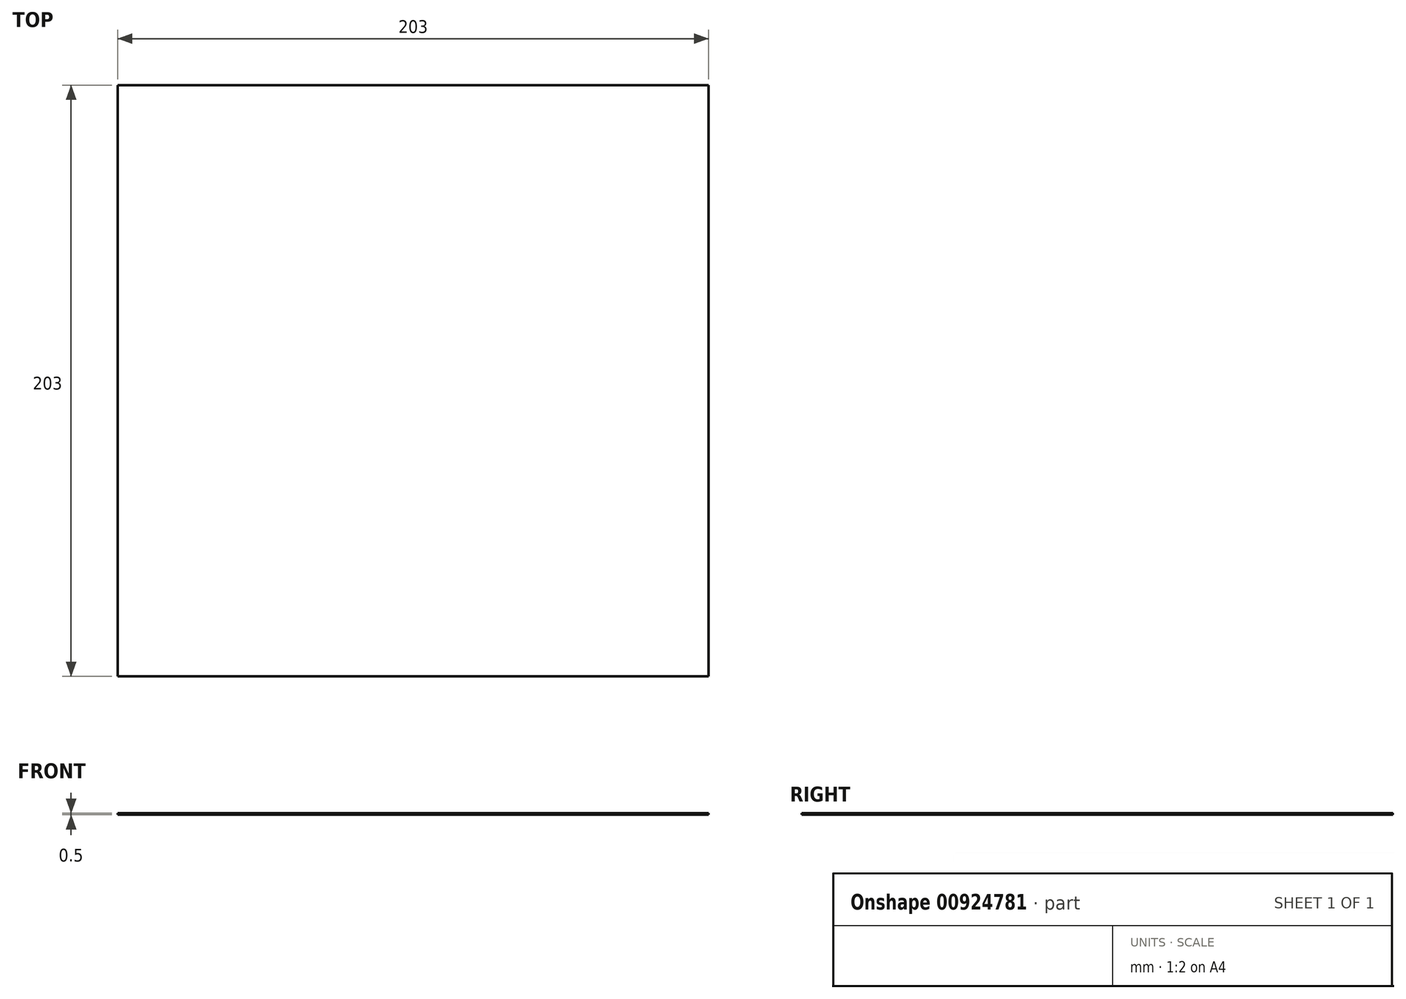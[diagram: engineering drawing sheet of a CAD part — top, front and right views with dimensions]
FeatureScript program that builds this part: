
annotation { "Feature Type Name" : "Feature", "Feature Type Description" : "" }
export const myFeature = defineFeature(function(context is Context, id is Id, definition is map)
    precondition{}
    {
        {
            var Q0;
            Q0=qCreatedBy(makeId("Top.planeOp"),FACE);
            var sketch = newSketch(context, id + "F0", { "sketchPlane" : qUnion([Q0])});
            skLineSegment(sketch, "E0.bottom", {"start": v(-103.23, -87.38) * mm, "end": v(99.77, -87.38) * mm});
            skLineSegment(sketch, "E0.top", {"start": v(-103.23, 115.62) * mm, "end": v(99.77, 115.62) * mm});
            skLineSegment(sketch, "E0.left", {"start": v(-103.23, -87.38) * mm, "end": v(-103.23, 115.62) * mm});
            skLineSegment(sketch, "E0.right", {"start": v(99.77, -87.38) * mm, "end": v(99.77, 115.62) * mm});
            skSolve(sketch);
        }
        {
            var Q0;
            Q0 = qSketchRegion(id + "F0", true);
            extrude(context, id + "F1", {"entities" : qUnion([Q0]), "oppositeDirection" : true, "depth" : .5 * mm, "offsetDistance" : 25 * mm});
        }
    });
